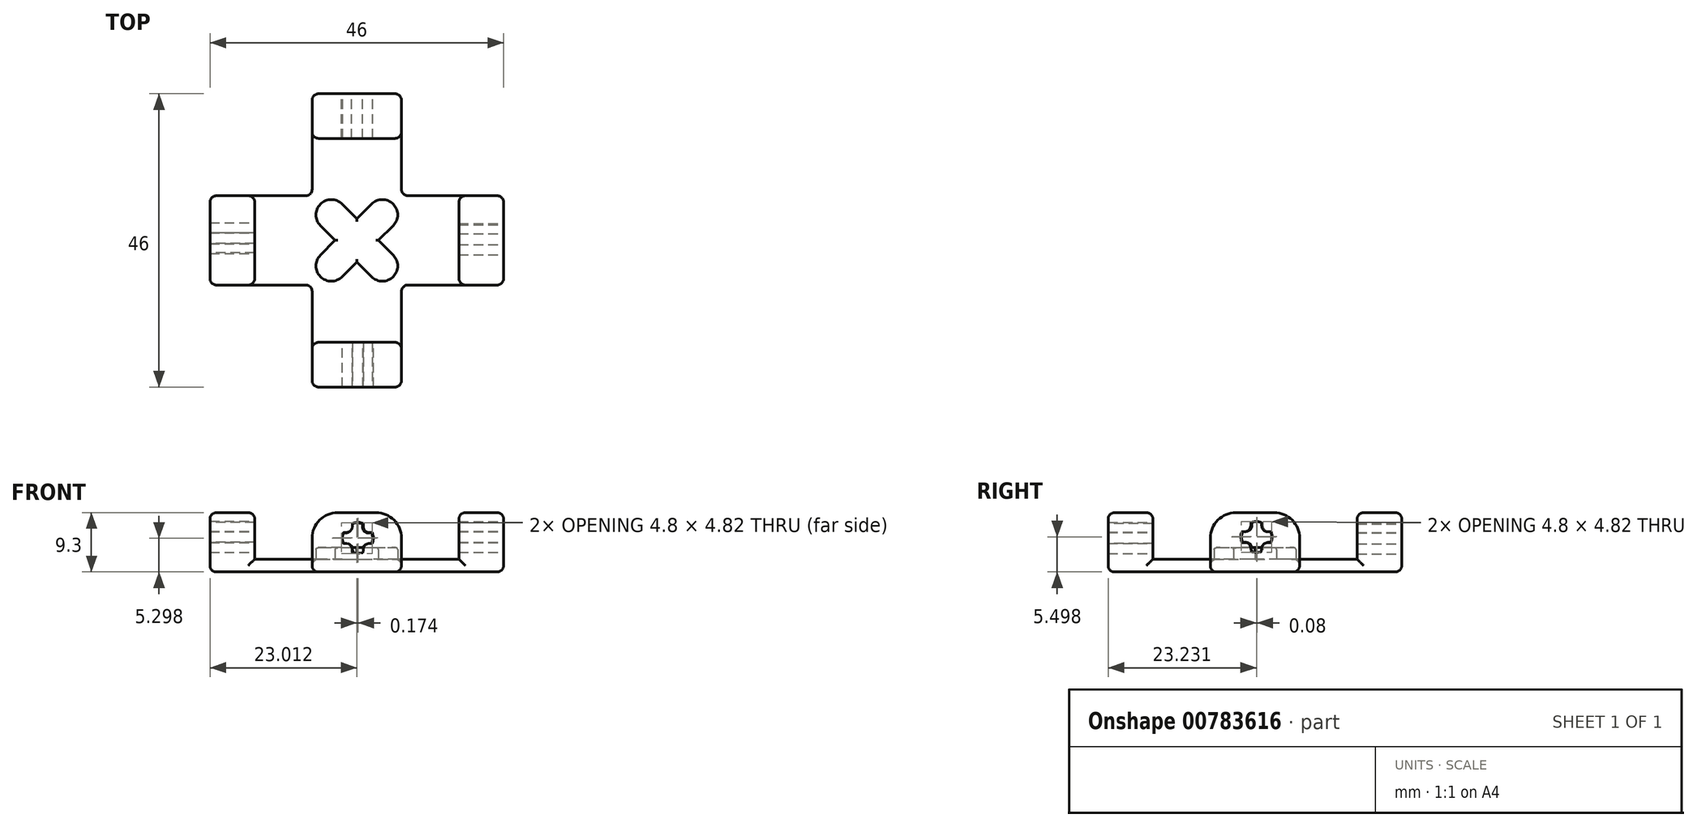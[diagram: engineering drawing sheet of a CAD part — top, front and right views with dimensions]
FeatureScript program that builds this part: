
annotation { "Feature Type Name" : "Feature", "Feature Type Description" : "" }
export const myFeature = defineFeature(function(context is Context, id is Id, definition is map)
    precondition{}
    {
        {
            var Q0;
            Q0=qCreatedBy(makeId("Top.planeOp"),FACE);
            var sketch = newSketch(context, id + "F0", { "sketchPlane" : qUnion([Q0])});
            skArc(sketch, "E0", {"start": v(1.7, 1.7) * mm, "mid": v(-1.7, 1.7) * mm, "end": v(-1.7, -1.7) * mm});
            skArc(sketch, "E1", {"start": v(9.7, -1.7) * mm, "mid": v(9.7, 1.7) * mm, "end": v(6.3, 1.7) * mm});
            skArc(sketch, "E2", {"start": v(-1.7, -6.3) * mm, "mid": v(-1.7, -9.7) * mm, "end": v(1.7, -9.7) * mm});
            skArc(sketch, "E3", {"start": v(6.3, -9.7) * mm, "mid": v(9.7, -9.7) * mm, "end": v(9.7, -6.3) * mm});
            skLineSegment(sketch, "E4", {"start": v(-1.7, -6.3) * mm, "end": v(0.6, -4) * mm});
            skLineSegment(sketch, "E5", {"start": v(1.7, -9.7) * mm, "end": v(4, -7.4) * mm});
            skLineSegment(sketch, "E6", {"start": v(1.7, 1.7) * mm, "end": v(4, -0.6) * mm});
            skLineSegment(sketch, "E7", {"start": v(-1.7, -1.7) * mm, "end": v(0.6, -4) * mm});
            skLineSegment(sketch, "E8.trimOffspring", {"start": v(4, -0.6) * mm, "end": v(6.3, 1.7) * mm});
            skLineSegment(sketch, "E9.trimOffspring", {"start": v(7.4, -4) * mm, "end": v(9.7, -6.3) * mm});
            skLineSegment(sketch, "E10.trimOffspring", {"start": v(7.4, -4) * mm, "end": v(9.7, -1.7) * mm});
            skLineSegment(sketch, "E11.trimOffspring", {"start": v(4, -7.4) * mm, "end": v(6.3, -9.7) * mm});
            skSolve(sketch);
        }
        {
            var Q0;
            Q0=qSketchRegion(id+"F0",true);
            extrude(context, id + "F1", {"entities" : qUnion([Q0]), "depth" : 1.8 * mm, "offsetDistance" : 25 * mm});
        }
        {
            var Q0;
            Q0=qCreatedBy(makeId("Top.planeOp"),FACE);
            var sketch = newSketch(context, id + "F2", { "sketchPlane" : qUnion([Q0])});
            skLineSegment(sketch, "E12", {"start": v(-3, 3) * mm, "end": v(-3, 19) * mm});
            skLineSegment(sketch, "E13", {"start": v(11, 19) * mm, "end": v(11, 3) * mm});
            skLineSegment(sketch, "E14", {"start": v(-3, 19) * mm, "end": v(11, 19) * mm});
            skLineSegment(sketch, "E15", {"start": v(-3, -27) * mm, "end": v(-3, -11) * mm});
            skLineSegment(sketch, "E16", {"start": v(11, -27) * mm, "end": v(11, -11) * mm});
            skLineSegment(sketch, "E17", {"start": v(-3, -27) * mm, "end": v(11, -27) * mm});
            skLineSegment(sketch, "E18", {"start": v(-3, 3) * mm, "end": v(-19, 3) * mm});
            skLineSegment(sketch, "E19", {"start": v(-3, -11) * mm, "end": v(-19, -11) * mm});
            skLineSegment(sketch, "E20", {"start": v(11, 3) * mm, "end": v(27, 3) * mm});
            skLineSegment(sketch, "E21", {"start": v(11, -11) * mm, "end": v(27, -11) * mm});
            skLineSegment(sketch, "E22", {"start": v(-19, 3) * mm, "end": v(-19, -11) * mm});
            skLineSegment(sketch, "E23", {"start": v(27, 3) * mm, "end": v(27, -11) * mm});
            skLineSegment(sketch, "E24", {"start": v(0, 0) * mm, "end": v(8.01, -8.01) * mm});
            skLineSegment(sketch, "E25", {"start": v(0.01, -7.99) * mm, "end": v(8, 0) * mm});
            skPoint(sketch, "E26", {"position": v(4, -4) * mm});
            skPoint(sketch, "E27", {"position": v(-19, -4) * mm});
            skPoint(sketch, "E28", {"position": v(4, 19) * mm});
            skLineSegment(sketch, "E29.bottom", {"start": v(-12, 12) * mm, "end": v(20, 12) * mm});
            skLineSegment(sketch, "E29.top", {"start": v(-12, -20) * mm, "end": v(20, -20) * mm});
            skLineSegment(sketch, "E29.left", {"start": v(-12, 12) * mm, "end": v(-12, -20) * mm});
            skLineSegment(sketch, "E29.right", {"start": v(20, 12) * mm, "end": v(20, -20) * mm});
            skPoint(sketch, "E30", {"position": v(-12, -4) * mm});
            skPoint(sketch, "E31", {"position": v(20, -4) * mm});
            skPoint(sketch, "E32", {"position": v(4, 12) * mm});
            skSolve(sketch);
        }
        {
            var Q0;
            Q0=makeQuery(id+"F2.imprint","IMPRINT",FACE,{"disambiguationData":[TD([[makeQuery(id+"F2.imprint","IMPRINT",EDGE,{"derivedFrom":sQuery(id+"F2.wireOp",EDGE,"E12")}),-1.0]])]});
            var Q1;
            {var subQ14=sQuery(id+"F2.wireOp",EDGE,"E12");var subQ18=sQuery(id+"F2.wireOp",EDGE,"E18");var subQ19=makeQuery(id+"F2.imprint","INTERSECT",VERTEX,{"derivedFrom":[subQ14,subQ18]});Q1=makeQuery(id+"F2.imprint","IMPRINT",FACE,{"disambiguationData":[TD([[makeQuery(id+"F2.imprint","IMPRINT",EDGE,{"disambiguationData":[TD([[subQ19,-1.0]])],"derivedFrom":subQ14}),-1.0]])]});}
            var Q2;
            {var subQ0=sQuery(id+"F2.wireOp",EDGE,"E23");Q2=makeQuery(id+"F2.imprint","IMPRINT",FACE,{"disambiguationData":[TD([[makeQuery(id+"F2.imprint","IMPRINT",EDGE,{"derivedFrom":subQ0}),-1.0]])]});}
            var Q3;
            {var subQ0=sQuery(id+"F2.wireOp",EDGE,"E17");Q3=makeQuery(id+"F2.imprint","IMPRINT",FACE,{"disambiguationData":[TD([[makeQuery(id+"F2.imprint","IMPRINT",EDGE,{"derivedFrom":subQ0}),1.0]])]});}
            var Q4;
            {var subQ0=sQuery(id+"F2.wireOp",EDGE,"E22");Q4=makeQuery(id+"F2.imprint","IMPRINT",FACE,{"disambiguationData":[TD([[makeQuery(id+"F2.imprint","IMPRINT",EDGE,{"derivedFrom":subQ0}),1.0]])]});}
            extrude(context, id + "F3", {"entities" : qUnion([Q0, Q1, Q2, Q3, Q4]), "operationType" : NewBodyOperationType.ADD, "oppositeDirection" : true, "depth" : 2 * mm, "offsetDistance" : 25 * mm});
        }
        {
            var Q0;
            Q0=qCreatedBy(makeId("Top.planeOp"),FACE);
            var sketch = newSketch(context, id + "F4", { "sketchPlane" : qUnion([Q0])});
            skLineSegment(sketch, "E33.bottom", {"start": v(-3, 19) * mm, "end": v(11, 19) * mm});
            skLineSegment(sketch, "E33.top", {"start": v(-3, 12) * mm, "end": v(11, 12) * mm});
            skLineSegment(sketch, "E33.left", {"start": v(-3, 19) * mm, "end": v(-3, 12) * mm});
            skLineSegment(sketch, "E33.right", {"start": v(11, 19) * mm, "end": v(11, 12) * mm});
            skLineSegment(sketch, "E34.bottom", {"start": v(20, 3) * mm, "end": v(27, 3) * mm});
            skLineSegment(sketch, "E34.top", {"start": v(20, -11) * mm, "end": v(27, -11) * mm});
            skLineSegment(sketch, "E34.left", {"start": v(20, 3) * mm, "end": v(20, -11) * mm});
            skLineSegment(sketch, "E34.right", {"start": v(27, 3) * mm, "end": v(27, -11) * mm});
            skLineSegment(sketch, "E35.bottom", {"start": v(-3, -20) * mm, "end": v(11, -20) * mm});
            skLineSegment(sketch, "E35.top", {"start": v(-3, -27) * mm, "end": v(11, -27) * mm});
            skLineSegment(sketch, "E35.left", {"start": v(-3, -20) * mm, "end": v(-3, -27) * mm});
            skLineSegment(sketch, "E35.right", {"start": v(11, -20) * mm, "end": v(11, -27) * mm});
            skLineSegment(sketch, "E36.bottom", {"start": v(-19, 3) * mm, "end": v(-12, 3) * mm});
            skLineSegment(sketch, "E36.top", {"start": v(-19, -11) * mm, "end": v(-12, -11) * mm});
            skLineSegment(sketch, "E36.left", {"start": v(-19, 3) * mm, "end": v(-19, -11) * mm});
            skLineSegment(sketch, "E36.right", {"start": v(-12, 3) * mm, "end": v(-12, -11) * mm});
            skPoint(sketch, "E37", {"position": v(4, 12) * mm});
            skLineSegment(sketch, "E38", {"start": v(-12, 12) * mm, "end": v(20, 12) * mm});
            skLineSegment(sketch, "E39", {"start": v(20, 12) * mm, "end": v(20, -20) * mm});
            skLineSegment(sketch, "E40", {"start": v(20, -20) * mm, "end": v(-12, -20) * mm});
            skLineSegment(sketch, "E41", {"start": v(-12, 12) * mm, "end": v(-12, -20) * mm});
            skPoint(sketch, "E42", {"position": v(20, -4) * mm});
            skSolve(sketch);
        }
        {
            var Q0;
            Q0=makeQuery(id+"F4.imprint","IMPRINT",FACE,{"disambiguationData":[TD([[makeQuery(id+"F4.imprint","IMPRINT",EDGE,{"derivedFrom":sQuery(id+"F4.wireOp",EDGE,"E33.bottom")}),-1.0]])]});
            var Q1;
            Q1=makeQuery(id+"F4.imprint","IMPRINT",FACE,{"disambiguationData":[TD([[makeQuery(id+"F4.imprint","IMPRINT",EDGE,{"derivedFrom":sQuery(id+"F4.wireOp",EDGE,"E34.bottom")}),-1.0]])]});
            var Q2;
            Q2=makeQuery(id+"F4.imprint","IMPRINT",FACE,{"disambiguationData":[TD([[makeQuery(id+"F4.imprint","IMPRINT",EDGE,{"derivedFrom":sQuery(id+"F4.wireOp",EDGE,"E35.bottom")}),-1.0]])]});
            var Q3;
            Q3=makeQuery(id+"F4.imprint","IMPRINT",FACE,{"disambiguationData":[TD([[makeQuery(id+"F4.imprint","IMPRINT",EDGE,{"derivedFrom":sQuery(id+"F4.wireOp",EDGE,"E36.bottom")}),-1.0]])]});
            extrude(context, id + "F5", {"entities" : qUnion([Q0, Q1, Q2, Q3]), "operationType" : NewBodyOperationType.ADD, "depth" : 7.3 * mm, "offsetDistance" : 25 * mm});
        }
        {
            var Q0;
            Q0=makeQuery(id+"F5.opExtrude","CAP_EDGE",EDGE,{"disambiguationData":[OSD([sQuery(id+"F4.wireOp",EDGE,"E36.top")])],"isStart":false});
            var Q1;
            Q1=makeQuery(id+"F5.opExtrude","CAP_EDGE",EDGE,{"disambiguationData":[OSD([sQuery(id+"F4.wireOp",EDGE,"E36.bottom")])],"isStart":false});
            var Q2;
            Q2=makeQuery(id+"F5.opExtrude","CAP_EDGE",EDGE,{"disambiguationData":[OSD([sQuery(id+"F4.wireOp",EDGE,"E33.left")])],"isStart":false});
            var Q3;
            Q3=makeQuery(id+"F5.opExtrude","CAP_EDGE",EDGE,{"disambiguationData":[OSD([sQuery(id+"F4.wireOp",EDGE,"E33.right")])],"isStart":false});
            var Q4;
            Q4=makeQuery(id+"F5.opExtrude","CAP_EDGE",EDGE,{"disambiguationData":[OSD([sQuery(id+"F4.wireOp",EDGE,"E34.bottom")])],"isStart":false});
            var Q5;
            Q5=makeQuery(id+"F5.opExtrude","CAP_EDGE",EDGE,{"disambiguationData":[OSD([sQuery(id+"F4.wireOp",EDGE,"E34.top")])],"isStart":false});
            var Q6;
            Q6=makeQuery(id+"F5.opExtrude","CAP_EDGE",EDGE,{"disambiguationData":[OSD([sQuery(id+"F4.wireOp",EDGE,"E35.right")])],"isStart":false});
            var Q7;
            Q7=makeQuery(id+"F5.opExtrude","CAP_EDGE",EDGE,{"disambiguationData":[OSD([sQuery(id+"F4.wireOp",EDGE,"E35.left")])],"isStart":false});
            fillet(context, id + "F6", {"entities" : qUnion([Q0, Q1, Q2, Q3, Q4, Q5, Q6, Q7]), "radius" : 4 * mm, "tangentPropagation" : true, "allowEdgeOverflow" : false});
        }
        {
            var Q0;
            Q0=makeQuery(id+"F3.opExtrude","SWEPT_EDGE",EDGE,{"disambiguationData":[OSD([sQuery(id+"F2.wireOp",EDGE,"E13"),sQuery(id+"F2.wireOp",EDGE,"E20")])]});
            var Q1;
            Q1=makeQuery(id+"F3.opExtrude","SWEPT_EDGE",EDGE,{"disambiguationData":[OSD([sQuery(id+"F2.wireOp",EDGE,"E16"),sQuery(id+"F2.wireOp",EDGE,"E21")])]});
            var Q2;
            Q2=makeQuery(id+"F3.opExtrude","SWEPT_EDGE",EDGE,{"disambiguationData":[OSD([sQuery(id+"F2.wireOp",EDGE,"E15"),sQuery(id+"F2.wireOp",EDGE,"E19")])]});
            var Q3;
            Q3=makeQuery(id+"F3.opExtrude","SWEPT_EDGE",EDGE,{"disambiguationData":[OSD([sQuery(id+"F2.wireOp",EDGE,"E12"),sQuery(id+"F2.wireOp",EDGE,"E18")])]});
            fillet(context, id + "F7", {"entities" : qUnion([Q0, Q1, Q2, Q3]), "radius" : 1 * mm, "tangentPropagation" : true, "allowEdgeOverflow" : false});
        }
        {
            var Q0;
            Q0=makeQuery(id+"F5.opExtrude","CAP_EDGE",EDGE,{"disambiguationData":[OSD([sQuery(id+"F4.wireOp",EDGE,"E33.top")])],"isStart":false});
            var Q1;
            Q1=makeQuery(id+"F3.opExtrude","CAP_EDGE",EDGE,{"disambiguationData":[OSD([sQuery(id+"F2.wireOp",EDGE,"E12")])],"isStart":true});
            var Q2;
            Q2=makeQuery(id+"F3.opExtrude","CAP_EDGE",EDGE,{"disambiguationData":[OSD([sQuery(id+"F2.wireOp",EDGE,"E13")])],"isStart":true});
            var Q3;
            Q3=makeQuery(id+"F3.opExtrude","CAP_EDGE",EDGE,{"disambiguationData":[OSD([sQuery(id+"F2.wireOp",EDGE,"E20")])],"isStart":true});
            var Q4;
            Q4=makeQuery(id+"F3.opExtrude","CAP_EDGE",EDGE,{"disambiguationData":[OSD([sQuery(id+"F2.wireOp",EDGE,"E21")])],"isStart":true});
            var Q5;
            Q5=makeQuery(id+"F3.opExtrude","CAP_EDGE",EDGE,{"disambiguationData":[OSD([sQuery(id+"F2.wireOp",EDGE,"E16")])],"isStart":true});
            var Q6;
            Q6=makeQuery(id+"F3.opExtrude","CAP_EDGE",EDGE,{"disambiguationData":[OSD([sQuery(id+"F2.wireOp",EDGE,"E15")])],"isStart":true});
            var Q7;
            Q7=makeQuery(id+"F3.opExtrude","CAP_EDGE",EDGE,{"disambiguationData":[OSD([sQuery(id+"F2.wireOp",EDGE,"E19")])],"isStart":true});
            var Q8;
            Q8=makeQuery(id+"F5.opExtrude","SWEPT_EDGE",EDGE,{"disambiguationData":[OSD([sQuery(id+"F4.wireOp",EDGE,"E36.top"),sQuery(id+"F4.wireOp",EDGE,"E36.right"),sQuery(id+"F4.wireOp",EDGE,"E41")])]});
            var Q9;
            Q9=makeQuery(id+"F6.opFillet","BLEND_EDGE",EDGE,{"blendedFrom":[makeQuery(id+"F5.opExtrude","CAP_EDGE",EDGE,{"disambiguationData":[OSD([sQuery(id+"F4.wireOp",EDGE,"E36.top")])],"isStart":false}),makeQuery(id+"F5.opExtrude","SWEPT_FACE",FACE,{"disambiguationData":[OSD([sQuery(id+"F4.wireOp",EDGE,"E36.right")])]})],"blendedInto":[makeQuery(id+"F5.opExtrude","SWEPT_FACE",FACE,{"disambiguationData":[OSD([sQuery(id+"F4.wireOp",EDGE,"E36.right")])]})]});
            var Q10;
            Q10=makeQuery(id+"F3.opExtrude","CAP_EDGE",EDGE,{"disambiguationData":[OSD([sQuery(id+"F2.wireOp",EDGE,"E18")])],"isStart":true});
            var Q11;
            Q11=makeQuery(id+"F6.opFillet","BLEND_EDGE",EDGE,{"blendedFrom":[makeQuery(id+"F5.opExtrude","CAP_EDGE",EDGE,{"disambiguationData":[OSD([sQuery(id+"F4.wireOp",EDGE,"E35.left")])],"isStart":false}),makeQuery(id+"F5.opExtrude","SWEPT_FACE",FACE,{"disambiguationData":[OSD([sQuery(id+"F4.wireOp",EDGE,"E35.bottom")])]})],"blendedInto":[makeQuery(id+"F5.opExtrude","SWEPT_FACE",FACE,{"disambiguationData":[OSD([sQuery(id+"F4.wireOp",EDGE,"E35.bottom")])]})]});
            var Q12;
            Q12=makeQuery(id+"F5.opExtrude","CAP_EDGE",EDGE,{"disambiguationData":[OSD([sQuery(id+"F4.wireOp",EDGE,"E34.left")])],"isStart":false});
            fillet(context, id + "F8", {"entities" : qUnion([Q0, Q1, Q2, Q3, Q4, Q5, Q6, Q7, Q8, Q9, Q10, Q11, Q12]), "radius" : 1 * mm, "tangentPropagation" : true, "allowEdgeOverflow" : false});
        }
        {
            var Q0;
            Q0=makeQuery(id+"F3.opExtrude","CAP_EDGE",EDGE,{"disambiguationData":[OSD([sQuery(id+"F2.wireOp",EDGE,"E22")])],"isStart":false});
            var Q1;
            Q1=makeQuery(id+"F3.opExtrude","CAP_EDGE",EDGE,{"disambiguationData":[OSD([sQuery(id+"F2.wireOp",EDGE,"E19")])],"isStart":false});
            var Q2;
            Q2=makeQuery(id+"F3.opExtrude","CAP_EDGE",EDGE,{"disambiguationData":[OSD([sQuery(id+"F2.wireOp",EDGE,"E15")])],"isStart":false});
            var Q3;
            Q3=makeQuery(id+"F3.opExtrude","CAP_EDGE",EDGE,{"disambiguationData":[OSD([sQuery(id+"F2.wireOp",EDGE,"E17")])],"isStart":false});
            var Q4;
            Q4=makeQuery(id+"F3.opExtrude","CAP_EDGE",EDGE,{"disambiguationData":[OSD([sQuery(id+"F2.wireOp",EDGE,"E16")])],"isStart":false});
            var Q5;
            Q5=makeQuery(id+"F3.opExtrude","CAP_EDGE",EDGE,{"disambiguationData":[OSD([sQuery(id+"F2.wireOp",EDGE,"E21")])],"isStart":false});
            var Q6;
            Q6=makeQuery(id+"F3.opExtrude","CAP_EDGE",EDGE,{"disambiguationData":[OSD([sQuery(id+"F2.wireOp",EDGE,"E23")])],"isStart":false});
            var Q7;
            Q7=makeQuery(id+"F3.opExtrude","CAP_EDGE",EDGE,{"disambiguationData":[OSD([sQuery(id+"F2.wireOp",EDGE,"E20")])],"isStart":false});
            var Q8;
            Q8=makeQuery(id+"F3.opExtrude","CAP_EDGE",EDGE,{"disambiguationData":[OSD([sQuery(id+"F2.wireOp",EDGE,"E13")])],"isStart":false});
            var Q9;
            Q9=makeQuery(id+"F3.opExtrude","CAP_EDGE",EDGE,{"disambiguationData":[OSD([sQuery(id+"F2.wireOp",EDGE,"E14")])],"isStart":false});
            var Q10;
            Q10=makeQuery(id+"F3.opExtrude","CAP_EDGE",EDGE,{"disambiguationData":[OSD([sQuery(id+"F2.wireOp",EDGE,"E12")])],"isStart":false});
            var Q11;
            Q11=makeQuery(id+"F3.opExtrude","CAP_EDGE",EDGE,{"disambiguationData":[OSD([sQuery(id+"F2.wireOp",EDGE,"E18")])],"isStart":false});
            var Q12;
            Q12=makeQuery(id+"F5.boolean.opBoolean","MERGE",EDGE,{"derivedFrom":[makeQuery(id+"F3.opExtrude","SWEPT_EDGE",EDGE,{"disambiguationData":[OSD([sQuery(id+"F2.wireOp",EDGE,"E16"),sQuery(id+"F2.wireOp",EDGE,"E17")])]}),makeQuery(id+"F5.opExtrude","SWEPT_EDGE",EDGE,{"disambiguationData":[OSD([sQuery(id+"F4.wireOp",EDGE,"E35.top"),sQuery(id+"F4.wireOp",EDGE,"E35.right")])]})]});
            var Q13;
            Q13=makeQuery(id+"F5.boolean.opBoolean","MERGE",EDGE,{"derivedFrom":[makeQuery(id+"F3.opExtrude","SWEPT_EDGE",EDGE,{"disambiguationData":[OSD([sQuery(id+"F2.wireOp",EDGE,"E19"),sQuery(id+"F2.wireOp",EDGE,"E22")])]}),makeQuery(id+"F5.opExtrude","SWEPT_EDGE",EDGE,{"disambiguationData":[OSD([sQuery(id+"F4.wireOp",EDGE,"E36.top"),sQuery(id+"F4.wireOp",EDGE,"E36.left")])]})]});
            var Q14;
            Q14=makeQuery(id+"F5.boolean.opBoolean","MERGE",EDGE,{"derivedFrom":[makeQuery(id+"F3.opExtrude","SWEPT_EDGE",EDGE,{"disambiguationData":[OSD([sQuery(id+"F2.wireOp",EDGE,"E13"),sQuery(id+"F2.wireOp",EDGE,"E14")])]}),makeQuery(id+"F5.opExtrude","SWEPT_EDGE",EDGE,{"disambiguationData":[OSD([sQuery(id+"F4.wireOp",EDGE,"E33.bottom"),sQuery(id+"F4.wireOp",EDGE,"E33.right")])]})]});
            var Q15;
            Q15=makeQuery(id+"F5.boolean.opBoolean","MERGE",EDGE,{"derivedFrom":[makeQuery(id+"F3.opExtrude","SWEPT_EDGE",EDGE,{"disambiguationData":[OSD([sQuery(id+"F2.wireOp",EDGE,"E21"),sQuery(id+"F2.wireOp",EDGE,"E23")])]}),makeQuery(id+"F5.opExtrude","SWEPT_EDGE",EDGE,{"disambiguationData":[OSD([sQuery(id+"F4.wireOp",EDGE,"E34.top"),sQuery(id+"F4.wireOp",EDGE,"E34.right")])]})]});
            var Q16;
            Q16=makeQuery(id+"F6.opFillet","BLEND_EDGE",EDGE,{"blendedFrom":[makeQuery(id+"F5.opExtrude","CAP_EDGE",EDGE,{"disambiguationData":[OSD([sQuery(id+"F4.wireOp",EDGE,"E33.right")])],"isStart":false}),makeQuery(id+"F5.boolean.opBoolean","MERGE",FACE,{"derivedFrom":[makeQuery(id+"F3.opExtrude","SWEPT_FACE",FACE,{"disambiguationData":[OSD([sQuery(id+"F2.wireOp",EDGE,"E14")])]}),makeQuery(id+"F5.opExtrude","SWEPT_FACE",FACE,{"disambiguationData":[OSD([sQuery(id+"F4.wireOp",EDGE,"E33.bottom")])]})]})],"blendedInto":[makeQuery(id+"F5.boolean.opBoolean","MERGE",FACE,{"derivedFrom":[makeQuery(id+"F3.opExtrude","SWEPT_FACE",FACE,{"disambiguationData":[OSD([sQuery(id+"F2.wireOp",EDGE,"E14")])]}),makeQuery(id+"F5.opExtrude","SWEPT_FACE",FACE,{"disambiguationData":[OSD([sQuery(id+"F4.wireOp",EDGE,"E33.bottom")])]})]})]});
            var Q17;
            Q17=makeQuery(id+"F5.opExtrude","CAP_EDGE",EDGE,{"disambiguationData":[OSD([sQuery(id+"F4.wireOp",EDGE,"E33.bottom")])],"isStart":false});
            var Q18;
            Q18=makeQuery(id+"F6.opFillet","BLEND_EDGE",EDGE,{"blendedFrom":[makeQuery(id+"F5.opExtrude","CAP_EDGE",EDGE,{"disambiguationData":[OSD([sQuery(id+"F4.wireOp",EDGE,"E33.left")])],"isStart":false}),makeQuery(id+"F5.boolean.opBoolean","MERGE",FACE,{"derivedFrom":[makeQuery(id+"F3.opExtrude","SWEPT_FACE",FACE,{"disambiguationData":[OSD([sQuery(id+"F2.wireOp",EDGE,"E14")])]}),makeQuery(id+"F5.opExtrude","SWEPT_FACE",FACE,{"disambiguationData":[OSD([sQuery(id+"F4.wireOp",EDGE,"E33.bottom")])]})]})],"blendedInto":[makeQuery(id+"F5.boolean.opBoolean","MERGE",FACE,{"derivedFrom":[makeQuery(id+"F3.opExtrude","SWEPT_FACE",FACE,{"disambiguationData":[OSD([sQuery(id+"F2.wireOp",EDGE,"E14")])]}),makeQuery(id+"F5.opExtrude","SWEPT_FACE",FACE,{"disambiguationData":[OSD([sQuery(id+"F4.wireOp",EDGE,"E33.bottom")])]})]})]});
            var Q19;
            Q19=makeQuery(id+"F5.boolean.opBoolean","MERGE",EDGE,{"derivedFrom":[makeQuery(id+"F3.opExtrude","SWEPT_EDGE",EDGE,{"disambiguationData":[OSD([sQuery(id+"F2.wireOp",EDGE,"E12"),sQuery(id+"F2.wireOp",EDGE,"E14")])]}),makeQuery(id+"F5.opExtrude","SWEPT_EDGE",EDGE,{"disambiguationData":[OSD([sQuery(id+"F4.wireOp",EDGE,"E33.bottom"),sQuery(id+"F4.wireOp",EDGE,"E33.left")])]})]});
            var Q20;
            Q20=makeQuery(id+"F6.opFillet","BLEND_EDGE",EDGE,{"blendedFrom":[makeQuery(id+"F5.opExtrude","CAP_EDGE",EDGE,{"disambiguationData":[OSD([sQuery(id+"F4.wireOp",EDGE,"E34.top")])],"isStart":false}),makeQuery(id+"F5.boolean.opBoolean","MERGE",FACE,{"derivedFrom":[makeQuery(id+"F3.opExtrude","SWEPT_FACE",FACE,{"disambiguationData":[OSD([sQuery(id+"F2.wireOp",EDGE,"E23")])]}),makeQuery(id+"F5.opExtrude","SWEPT_FACE",FACE,{"disambiguationData":[OSD([sQuery(id+"F4.wireOp",EDGE,"E34.right")])]})]})],"blendedInto":[makeQuery(id+"F5.boolean.opBoolean","MERGE",FACE,{"derivedFrom":[makeQuery(id+"F3.opExtrude","SWEPT_FACE",FACE,{"disambiguationData":[OSD([sQuery(id+"F2.wireOp",EDGE,"E23")])]}),makeQuery(id+"F5.opExtrude","SWEPT_FACE",FACE,{"disambiguationData":[OSD([sQuery(id+"F4.wireOp",EDGE,"E34.right")])]})]})]});
            fillet(context, id + "F9", {"entities" : qUnion([Q0, Q1, Q2, Q3, Q4, Q5, Q6, Q7, Q8, Q9, Q10, Q11, Q12, Q13, Q14, Q15, Q16, Q17, Q18, Q19, Q20]), "radius" : 1 * mm, "tangentPropagation" : true, "allowEdgeOverflow" : false});
        }
        {
            var Q0;
            Q0=makeQuery(id+"F1.opExtrude","CAP_EDGE",EDGE,{"disambiguationData":[OSD([sQuery(id+"F0.wireOp",EDGE,"E4")])],"isStart":false});
            var Q1;
            Q1=makeQuery(id+"F1.opExtrude","CAP_EDGE",EDGE,{"disambiguationData":[OSD([sQuery(id+"F0.wireOp",EDGE,"E7")])],"isStart":false});
            var Q2;
            Q2=makeQuery(id+"F1.opExtrude","CAP_EDGE",EDGE,{"disambiguationData":[OSD([sQuery(id+"F0.wireOp",EDGE,"E8.trimOffspring")])],"isStart":false});
            var Q3;
            Q3=makeQuery(id+"F1.opExtrude","CAP_EDGE",EDGE,{"disambiguationData":[OSD([sQuery(id+"F0.wireOp",EDGE,"E9.trimOffspring")])],"isStart":false});
            fillet(context, id + "F10", {"entities" : qUnion([Q0, Q1, Q2, Q3]), "radius" : 0.3 * mm, "tangentPropagation" : true, "allowEdgeOverflow" : false});
        }
        {
            var Q0;
            Q0=makeQuery(id+"F5.boolean.opBoolean","MERGE",FACE,{"derivedFrom":[makeQuery(id+"F3.opExtrude","SWEPT_FACE",FACE,{"disambiguationData":[OSD([sQuery(id+"F2.wireOp",EDGE,"E17")])]}),makeQuery(id+"F5.opExtrude","SWEPT_FACE",FACE,{"disambiguationData":[OSD([sQuery(id+"F4.wireOp",EDGE,"E35.top")])]})]});
            var sketch = newSketch(context, id + "F11", { "sketchPlane" : qUnion([Q0])});
            skFitSpline(sketch, "E43", {"points": [v(3.3, 5.6) * mm, v(4.18, 5.77) * mm, v(5, 5.6) * mm], "startDerivative": vector(1.75, 0.5) * mm, "endDerivative": vector(1.65, -0.5) * mm});
            skFitSpline(sketch, "E44", {"points": [v(5, 5.6) * mm, v(5, 5.04) * mm, v(5.15, 4.6) * mm, v(5.46, 4.3) * mm, v(5.8, 4.2) * mm, v(6.22, 4.18) * mm, v(6.42, 4.18) * mm, v(6.5, 3.94) * mm, v(6.58, 3.55) * mm, v(6.58, 3.21) * mm, v(6.54, 2.9) * mm, v(6.42, 2.48) * mm], "startDerivative": vector(-0.26, -5.18) * mm, "endDerivative": vector(-1.41, -4.37) * mm});
            skFitSpline(sketch, "E45", {"points": [v(3.3, 5.6) * mm, v(3.3, 5.3) * mm, v(3.3, 5.06) * mm, v(3.27, 4.87) * mm, v(3.1, 4.53) * mm, v(2.9, 4.35) * mm, v(2.64, 4.22) * mm, v(2.32, 4.18) * mm, v(1.88, 4.18) * mm, v(1.79, 3.9) * mm, v(1.73, 3.62) * mm, v(1.71, 3.29) * mm, v(1.74, 3) * mm, v(1.8, 2.73) * mm, v(1.88, 2.48) * mm, v(2.07, 2.48) * mm, v(2.39, 2.48) * mm, v(2.64, 2.45) * mm, v(2.82, 2.37) * mm, v(3.05, 2.2) * mm, v(3.16, 2.05) * mm, v(3.24, 1.87) * mm, v(3.3, 1.63) * mm, v(3.3, 1.38) * mm, v(3.3, 1.06) * mm, v(3.56, 0.98) * mm, v(3.9, 0.92) * mm, v(4.18, 0.9) * mm, v(4.45, 0.93) * mm, v(4.82, 1) * mm, v(5, 1.06) * mm, v(5, 1.38) * mm, v(5, 1.66) * mm, v(5.1, 1.99) * mm, v(5.24, 2.18) * mm, v(5.5, 2.38) * mm, v(5.92, 2.48) * mm, v(6.42, 2.48) * mm], "startDerivative": vector(-0.02, -10.87) * mm, "endDerivative": vector(14.17, -0.52) * mm});
            skSolve(sketch);
        }
        {
            var Q0;
            Q0=makeQuery(id+"F11.imprint","IMPRINT",FACE,{"disambiguationData":[TD([[makeQuery(id+"F11.imprint","IMPRINT",EDGE,{"derivedFrom":sQuery(id+"F11.wireOp",EDGE,"E43")}),-1.0]])]});
            extrude(context, id + "F12", {"entities" : qUnion([Q0]), "operationType" : NewBodyOperationType.REMOVE, "oppositeDirection" : true, "depth" : 11.1 * mm, "offsetDistance" : 25 * mm});
        }
        {
            var Q0;
            Q0=makeQuery(id+"F5.boolean.opBoolean","MERGE",FACE,{"derivedFrom":[makeQuery(id+"F3.opExtrude","SWEPT_FACE",FACE,{"disambiguationData":[OSD([sQuery(id+"F2.wireOp",EDGE,"E23")])]}),makeQuery(id+"F5.opExtrude","SWEPT_FACE",FACE,{"disambiguationData":[OSD([sQuery(id+"F4.wireOp",EDGE,"E34.right")])]})]});
            var sketch = newSketch(context, id + "F13", { "sketchPlane" : qUnion([Q0])});
            skFitSpline(sketch, "E46", {"points": [v(-4.65, 5.74) * mm, v(-3.77, 5.9) * mm, v(-2.95, 5.74) * mm], "startDerivative": vector(1.75, 0.5) * mm, "endDerivative": vector(1.65, -0.5) * mm});
            skFitSpline(sketch, "E47", {"points": [v(-2.95, 5.74) * mm, v(-2.95, 5.18) * mm, v(-2.8, 4.74) * mm, v(-2.5, 4.44) * mm, v(-2.15, 4.33) * mm, v(-1.73, 4.32) * mm, v(-1.53, 4.32) * mm, v(-1.45, 4.08) * mm, v(-1.38, 3.7) * mm, v(-1.37, 3.35) * mm, v(-1.41, 3.03) * mm, v(-1.53, 2.62) * mm], "startDerivative": vector(-0.26, -5.18) * mm, "endDerivative": vector(-1.41, -4.37) * mm});
            skFitSpline(sketch, "E48", {"points": [v(-4.65, 5.74) * mm, v(-4.65, 5.45) * mm, v(-4.66, 5.2) * mm, v(-4.69, 5.01) * mm, v(-4.86, 4.67) * mm, v(-5.06, 4.49) * mm, v(-5.32, 4.36) * mm, v(-5.63, 4.32) * mm, v(-6.08, 4.32) * mm, v(-6.17, 4.04) * mm, v(-6.22, 3.75) * mm, v(-6.24, 3.43) * mm, v(-6.22, 3.14) * mm, v(-6.16, 2.87) * mm, v(-6.08, 2.62) * mm, v(-5.88, 2.62) * mm, v(-5.57, 2.62) * mm, v(-5.32, 2.58) * mm, v(-5.13, 2.5) * mm, v(-4.9, 2.33) * mm, v(-4.8, 2.2) * mm, v(-4.71, 2.01) * mm, v(-4.66, 1.76) * mm, v(-4.65, 1.52) * mm, v(-4.65, 1.2) * mm, v(-4.4, 1.12) * mm, v(-4.05, 1.06) * mm, v(-3.77, 1.05) * mm, v(-3.5, 1.06) * mm, v(-3.14, 1.14) * mm, v(-2.95, 1.2) * mm, v(-2.95, 1.52) * mm, v(-2.95, 1.8) * mm, v(-2.85, 2.12) * mm, v(-2.71, 2.32) * mm, v(-2.45, 2.52) * mm, v(-2.03, 2.62) * mm, v(-1.53, 2.62) * mm], "startDerivative": vector(-0.02, -10.87) * mm, "endDerivative": vector(14.17, -0.52) * mm});
            skSolve(sketch);
        }
        {
            var Q0;
            Q0=makeQuery(id+"F13.imprint","IMPRINT",FACE,{"disambiguationData":[TD([[makeQuery(id+"F13.imprint","IMPRINT",EDGE,{"derivedFrom":sQuery(id+"F13.wireOp",EDGE,"E46")}),-1.0]])]});
            extrude(context, id + "F14", {"entities" : qUnion([Q0]), "operationType" : NewBodyOperationType.REMOVE, "oppositeDirection" : true, "depth" : 8.3 * mm, "offsetDistance" : 25 * mm});
        }
        {
            var Q0;
            Q0=makeQuery(id+"F5.boolean.opBoolean","MERGE",FACE,{"derivedFrom":[makeQuery(id+"F3.opExtrude","SWEPT_FACE",FACE,{"disambiguationData":[OSD([sQuery(id+"F2.wireOp",EDGE,"E14")])]}),makeQuery(id+"F5.opExtrude","SWEPT_FACE",FACE,{"disambiguationData":[OSD([sQuery(id+"F4.wireOp",EDGE,"E33.bottom")])]})]});
            var sketch = newSketch(context, id + "F15", { "sketchPlane" : qUnion([Q0])});
            skFitSpline(sketch, "E49", {"points": [v(-4.9, 5.54) * mm, v(-4.01, 5.7) * mm, v(-3.2, 5.54) * mm], "startDerivative": vector(1.75, 0.5) * mm, "endDerivative": vector(1.65, -0.5) * mm});
            skFitSpline(sketch, "E50", {"points": [v(-3.2, 5.54) * mm, v(-3.2, 4.98) * mm, v(-3.05, 4.54) * mm, v(-2.73, 4.24) * mm, v(-2.4, 4.13) * mm, v(-1.98, 4.12) * mm, v(-1.78, 4.12) * mm, v(-1.7, 3.88) * mm, v(-1.62, 3.5) * mm, v(-1.61, 3.15) * mm, v(-1.65, 2.83) * mm, v(-1.78, 2.42) * mm], "startDerivative": vector(-0.26, -5.18) * mm, "endDerivative": vector(-1.41, -4.37) * mm});
            skFitSpline(sketch, "E51", {"points": [v(-4.9, 5.54) * mm, v(-4.9, 5.25) * mm, v(-4.9, 5) * mm, v(-4.93, 4.81) * mm, v(-5.1, 4.47) * mm, v(-5.3, 4.29) * mm, v(-5.56, 4.16) * mm, v(-5.88, 4.12) * mm, v(-6.32, 4.12) * mm, v(-6.4, 3.84) * mm, v(-6.47, 3.55) * mm, v(-6.49, 3.23) * mm, v(-6.46, 2.94) * mm, v(-6.4, 2.67) * mm, v(-6.32, 2.42) * mm, v(-6.12, 2.42) * mm, v(-5.8, 2.42) * mm, v(-5.56, 2.38) * mm, v(-5.37, 2.3) * mm, v(-5.15, 2.13) * mm, v(-5.04, 2) * mm, v(-4.95, 1.81) * mm, v(-4.9, 1.56) * mm, v(-4.9, 1.32) * mm, v(-4.9, 1) * mm, v(-4.64, 0.92) * mm, v(-4.3, 0.86) * mm, v(-4.01, 0.85) * mm, v(-3.75, 0.86) * mm, v(-3.38, 0.94) * mm, v(-3.2, 1) * mm, v(-3.2, 1.32) * mm, v(-3.2, 1.6) * mm, v(-3.1, 1.92) * mm, v(-2.96, 2.12) * mm, v(-2.69, 2.32) * mm, v(-2.27, 2.42) * mm, v(-1.78, 2.42) * mm], "startDerivative": vector(-0.02, -10.87) * mm, "endDerivative": vector(14.17, -0.52) * mm});
            skSolve(sketch);
        }
        {
            var Q0;
            Q0=makeQuery(id+"F15.imprint","IMPRINT",FACE,{"disambiguationData":[TD([[makeQuery(id+"F15.imprint","IMPRINT",EDGE,{"derivedFrom":sQuery(id+"F15.wireOp",EDGE,"E49")}),-1.0]])]});
            extrude(context, id + "F16", {"entities" : qUnion([Q0]), "operationType" : NewBodyOperationType.REMOVE, "oppositeDirection" : true, "depth" : 9.8 * mm, "offsetDistance" : 25 * mm});
        }
        {
            var Q0;
            Q0=makeQuery(id+"F5.boolean.opBoolean","MERGE",FACE,{"derivedFrom":[makeQuery(id+"F3.opExtrude","SWEPT_FACE",FACE,{"disambiguationData":[OSD([sQuery(id+"F2.wireOp",EDGE,"E22")])]}),makeQuery(id+"F5.opExtrude","SWEPT_FACE",FACE,{"disambiguationData":[OSD([sQuery(id+"F4.wireOp",EDGE,"E36.left")])]})]});
            var sketch = newSketch(context, id + "F17", { "sketchPlane" : qUnion([Q0])});
            skFitSpline(sketch, "E52", {"points": [v(2.8, 5.76) * mm, v(3.69, 5.93) * mm, v(4.5, 5.76) * mm], "startDerivative": vector(1.75, 0.5) * mm, "endDerivative": vector(1.65, -0.5) * mm});
            skFitSpline(sketch, "E53", {"points": [v(4.5, 5.76) * mm, v(4.5, 5.2) * mm, v(4.65, 4.76) * mm, v(4.97, 4.46) * mm, v(5.3, 4.35) * mm, v(5.72, 4.34) * mm, v(5.92, 4.34) * mm, v(6, 4.1) * mm, v(6.08, 3.71) * mm, v(6.09, 3.37) * mm, v(6.05, 3.06) * mm, v(5.92, 2.64) * mm], "startDerivative": vector(-0.26, -5.18) * mm, "endDerivative": vector(-1.41, -4.37) * mm});
            skFitSpline(sketch, "E54", {"points": [v(2.8, 5.76) * mm, v(2.8, 5.47) * mm, v(2.8, 5.22) * mm, v(2.77, 5.03) * mm, v(2.6, 4.7) * mm, v(2.4, 4.5) * mm, v(2.14, 4.38) * mm, v(1.82, 4.34) * mm, v(1.38, 4.34) * mm, v(1.3, 4.06) * mm, v(1.24, 3.78) * mm, v(1.22, 3.45) * mm, v(1.24, 3.16) * mm, v(1.3, 2.9) * mm, v(1.38, 2.64) * mm, v(1.58, 2.64) * mm, v(1.9, 2.64) * mm, v(2.14, 2.6) * mm, v(2.33, 2.53) * mm, v(2.55, 2.35) * mm, v(2.66, 2.21) * mm, v(2.75, 2.03) * mm, v(2.8, 1.79) * mm, v(2.8, 1.54) * mm, v(2.8, 1.22) * mm, v(3.06, 1.14) * mm, v(3.4, 1.08) * mm, v(3.69, 1.07) * mm, v(3.95, 1.09) * mm, v(4.32, 1.16) * mm, v(4.5, 1.22) * mm, v(4.5, 1.54) * mm, v(4.5, 1.82) * mm, v(4.6, 2.15) * mm, v(4.75, 2.34) * mm, v(5.01, 2.54) * mm, v(5.43, 2.64) * mm, v(5.92, 2.64) * mm], "startDerivative": vector(-0.02, -10.87) * mm, "endDerivative": vector(14.17, -0.52) * mm});
            skFitSpline(sketch, "E55", {"points": [v(13.1, 5.76) * mm, v(13.99, 5.93) * mm, v(14.8, 5.76) * mm], "startDerivative": vector(1.75, 0.5) * mm, "endDerivative": vector(1.65, -0.5) * mm});
            skFitSpline(sketch, "E56", {"points": [v(14.8, 5.76) * mm, v(14.8, 5.2) * mm, v(14.95, 4.76) * mm, v(15.27, 4.46) * mm, v(15.61, 4.35) * mm, v(16.03, 4.34) * mm, v(16.23, 4.34) * mm, v(16.3, 4.1) * mm, v(16.38, 3.71) * mm, v(16.4, 3.37) * mm, v(16.35, 3.06) * mm, v(16.23, 2.64) * mm], "startDerivative": vector(-0.26, -5.18) * mm, "endDerivative": vector(-1.41, -4.37) * mm});
            skFitSpline(sketch, "E57", {"points": [v(13.1, 5.76) * mm, v(13.1, 5.47) * mm, v(13.1, 5.22) * mm, v(13.07, 5.03) * mm, v(12.9, 4.7) * mm, v(12.7, 4.5) * mm, v(12.45, 4.38) * mm, v(12.13, 4.34) * mm, v(11.68, 4.34) * mm, v(11.6, 4.06) * mm, v(11.54, 3.78) * mm, v(11.52, 3.45) * mm, v(11.55, 3.16) * mm, v(11.6, 2.9) * mm, v(11.68, 2.64) * mm, v(11.88, 2.64) * mm, v(12.2, 2.64) * mm, v(12.44, 2.6) * mm, v(12.63, 2.53) * mm, v(12.85, 2.35) * mm, v(12.96, 2.21) * mm, v(13.05, 2.03) * mm, v(13.1, 1.79) * mm, v(13.1, 1.54) * mm, v(13.1, 1.22) * mm, v(13.36, 1.14) * mm, v(13.71, 1.08) * mm, v(13.99, 1.07) * mm, v(14.25, 1.09) * mm, v(14.62, 1.16) * mm, v(14.8, 1.22) * mm, v(14.8, 1.54) * mm, v(14.81, 1.82) * mm, v(14.91, 2.15) * mm, v(15.05, 2.34) * mm, v(15.32, 2.54) * mm, v(15.73, 2.64) * mm, v(16.23, 2.64) * mm], "startDerivative": vector(-0.02, -10.87) * mm, "endDerivative": vector(14.17, -0.52) * mm});
            skFitSpline(sketch, "E58", {"points": [v(22.64, 5.68) * mm, v(23.52, 5.85) * mm, v(24.34, 5.68) * mm], "startDerivative": vector(1.75, 0.5) * mm, "endDerivative": vector(1.65, -0.5) * mm});
            skFitSpline(sketch, "E59", {"points": [v(24.34, 5.68) * mm, v(24.34, 5.12) * mm, v(24.49, 4.69) * mm, v(24.8, 4.39) * mm, v(25.14, 4.27) * mm, v(25.56, 4.26) * mm, v(25.76, 4.26) * mm, v(25.84, 4.02) * mm, v(25.91, 3.64) * mm, v(25.92, 3.3) * mm, v(25.88, 2.98) * mm, v(25.76, 2.56) * mm], "startDerivative": vector(-0.26, -5.18) * mm, "endDerivative": vector(-1.41, -4.37) * mm});
            skFitSpline(sketch, "E60", {"points": [v(22.64, 5.68) * mm, v(22.64, 5.39) * mm, v(22.64, 5.14) * mm, v(22.6, 4.95) * mm, v(22.44, 4.61) * mm, v(22.24, 4.43) * mm, v(21.98, 4.3) * mm, v(21.66, 4.26) * mm, v(21.22, 4.26) * mm, v(21.13, 3.98) * mm, v(21.07, 3.7) * mm, v(21.05, 3.37) * mm, v(21.08, 3.08) * mm, v(21.13, 2.81) * mm, v(21.22, 2.56) * mm, v(21.41, 2.56) * mm, v(21.73, 2.56) * mm, v(21.97, 2.53) * mm, v(22.16, 2.45) * mm, v(22.38, 2.27) * mm, v(22.5, 2.13) * mm, v(22.58, 1.95) * mm, v(22.63, 1.7) * mm, v(22.64, 1.46) * mm, v(22.64, 1.14) * mm, v(22.9, 1.06) * mm, v(23.24, 1) * mm, v(23.52, 0.99) * mm, v(23.79, 1) * mm, v(24.15, 1.08) * mm, v(24.34, 1.14) * mm, v(24.34, 1.46) * mm, v(24.34, 1.74) * mm, v(24.44, 2.07) * mm, v(24.58, 2.26) * mm, v(24.85, 2.46) * mm, v(25.26, 2.56) * mm, v(25.76, 2.56) * mm], "startDerivative": vector(-0.02, -10.87) * mm, "endDerivative": vector(14.17, -0.52) * mm});
            skSolve(sketch);
        }
        {
            var Q0;
            Q0=makeQuery(id+"F17.imprint","IMPRINT",FACE,{"disambiguationData":[TD([[makeQuery(id+"F17.imprint","IMPRINT",EDGE,{"derivedFrom":sQuery(id+"F17.wireOp",EDGE,"E52")}),-1.0]])]});
            extrude(context, id + "F18", {"entities" : qUnion([Q0]), "operationType" : NewBodyOperationType.REMOVE, "oppositeDirection" : true, "depth" : 12.3 * mm, "offsetDistance" : 25 * mm});
        }
    });
